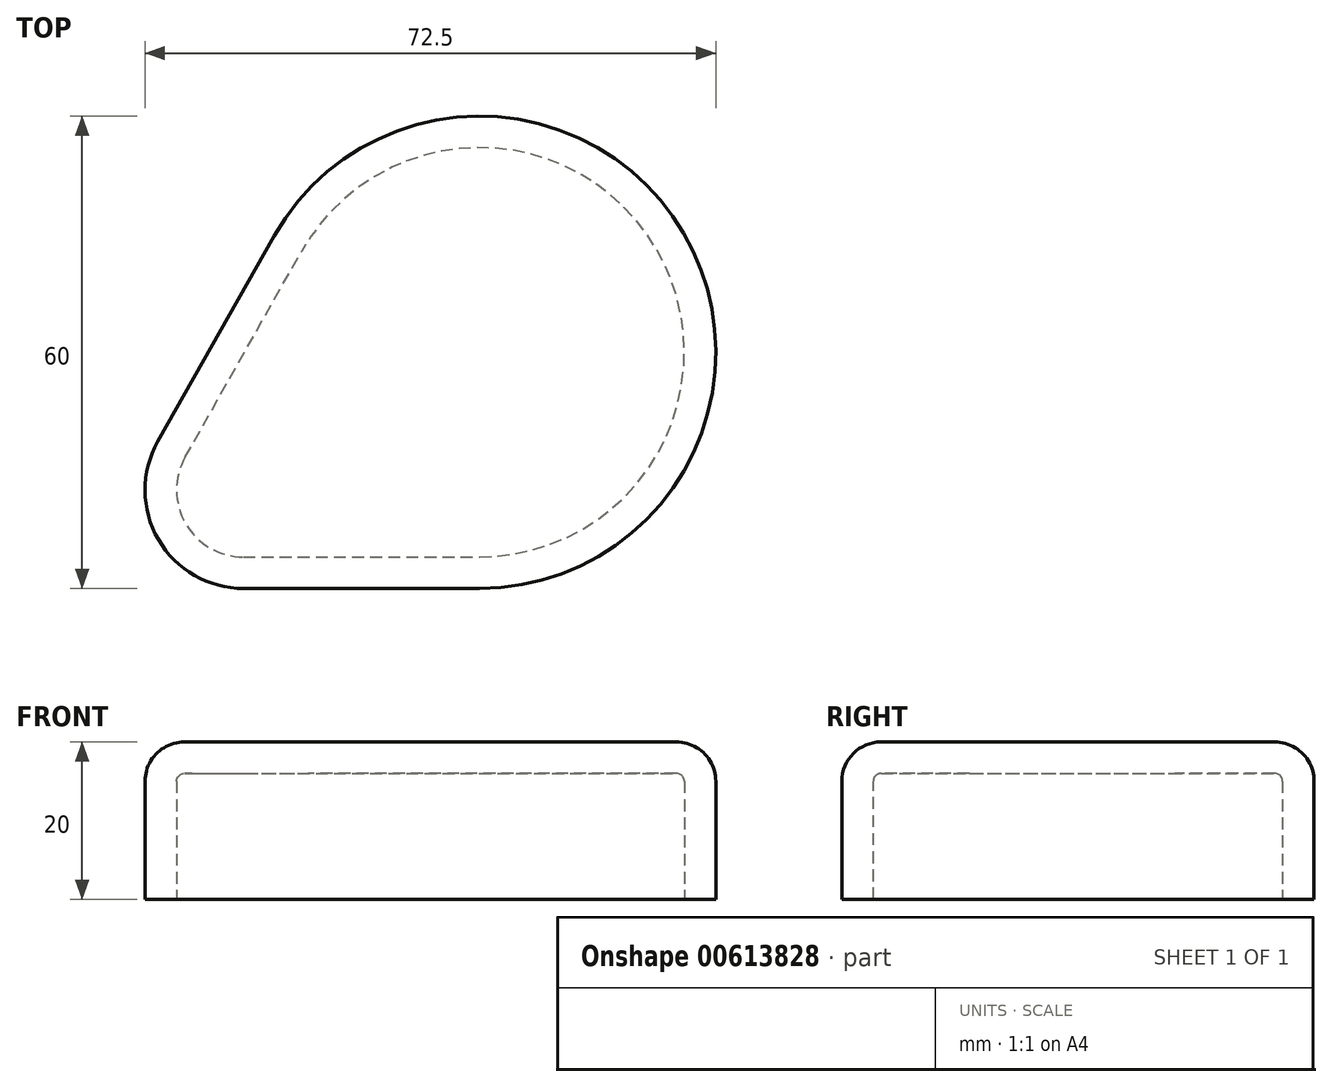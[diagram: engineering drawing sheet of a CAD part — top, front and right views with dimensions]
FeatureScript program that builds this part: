
annotation { "Feature Type Name" : "Feature", "Feature Type Description" : "" }
export const myFeature = defineFeature(function(context is Context, id is Id, definition is map)
    precondition{}
    {
        {
            var Q0;
            Q0=qCreatedBy(makeId("Top.planeOp"),FACE);
            var sketch = newSketch(context, id + "F0", { "sketchPlane" : qUnion([Q0])});
            skCircle(sketch, "E0", {"center": v(30, 30) * mm, "radius": 30 * mm});
            skCircle(sketch, "E1", {"center": v(0, 12.5) * mm, "radius": 12.5 * mm});
            skLineSegment(sketch, "E2", {"start": v(0, 0) * mm, "end": v(30, 0) * mm});
            skLineSegment(sketch, "E3", {"start": v(-10.88, 18.65) * mm, "end": v(3.89, 44.77) * mm});
            skLineSegment(sketch, "E4", {"start": v(0, 12.5) * mm, "end": v(30, 30) * mm, "construction": true});
            skLineSegment(sketch, "E5", {"start": v(30, 30) * mm, "end": v(60, 30) * mm, "construction": true});
            skLineSegment(sketch, "E6", {"start": v(60, 30) * mm, "end": v(60, 0) * mm, "construction": true});
            skLineSegment(sketch, "E7", {"start": v(60, 0) * mm, "end": v(0, 0) * mm, "construction": true});
            skSolve(sketch);
        }
        {
            var Q0;
            Q0 = qSketchRegion(id + "F0", true);
            var Q1;
            {var subQ0=sQuery(id+"F0.wireOp",EDGE,"E1");var subQ1=sQuery(id+"F0.wireOp",EDGE,"E0");var subQ2=makeQuery(id+"F0.imprint","INTERSECT",VERTEX,{"disambiguationData":[OD(0.0)],"derivedFrom":[subQ1,subQ0]});Q1=makeQuery(id+"F0.imprint","IMPRINT",FACE,{"disambiguationData":[TD([[makeQuery(id+"F0.imprint","IMPRINT",EDGE,{"disambiguationData":[TD([[subQ2,-1.0]])],"derivedFrom":subQ1}),1.0]])]});}
            extrude(context, id + "F1", {"entities" : qUnion([Q0, Q1]), "depth" : 20 * mm, "offsetDistance" : 25 * mm});
        }
        {
            var Q0;
            Q0=makeQuery(id+"F1.opExtrude","CAP_FACE",FACE,{"disambiguationData":[OSD([sQuery(id+"F0.wireOp",EDGE,"E0"),sQuery(id+"F0.wireOp",EDGE,"E1"),sQuery(id+"F0.wireOp",EDGE,"E2"),sQuery(id+"F0.wireOp",EDGE,"E3")])],"isStart":false});
            fillet(context, id + "F2", {"entities" : qUnion([Q0]), "tangentPropagation" : true, "radius" : 5 * mm, "defaultsChanged" : false, "vertexSettings" : [], "allowEdgeOverflow" : false});
        }
        {
            var Q0;
            Q0=makeQuery(id+"F1.opExtrude","CAP_FACE",FACE,{"disambiguationData":[OSD([sQuery(id+"F0.wireOp",EDGE,"E0"),sQuery(id+"F0.wireOp",EDGE,"E1"),sQuery(id+"F0.wireOp",EDGE,"E2"),sQuery(id+"F0.wireOp",EDGE,"E3")])],"isStart":true});
            shell(context, id + "F3", {"entities" : qUnion([Q0]), "thickness" : 4 * mm});
        }
    });
